# Revit family: GLIDER-SM_AUA03510130001
name_source: partatom
category: Lighting Fixtures
units: mm (PartAtom-declared; Revit-internal decimal feet)

## family parameters
Cut with Voids When Loaded = No
Host = Face
Light Source = Yes
OmniClass Number = 23.80.70.11.21
OmniClass Title = Emergency Lighting
Part Type = Normal
Room Calculation Point = No
Round Connector Dimension = Use Diameter
Shared = No

## types (5) — shared parameters
3D Content Provider = Mepros engineering
Apparent Load = 0 VA
Clevertronics_AS2293 Classification = C0=E4, C90=E4, C180=E2.5, C270=E3.2
Clevertronics_Applicable Standards = AS/NZS3820, CISPR15, AS/NZS2293.3
Clevertronics_Battery = 3.2V 1100mAh
Clevertronics_Battery Type = Lithium Iron Phosphate
Clevertronics_Body/Box (LxWxH mm) = 341mm x 60mm x 215mm
Clevertronics_Charger Method = Intelligent Current Limited Constant Voltage
Clevertronics_Construction = PC/ABS body with PC diffuser
Clevertronics_Diffuser = All pictograph directional inserts included in the box
Clevertronics_Earth Leakage = 0.42
Clevertronics_Emergency Driver = 8003552 : Emergency Driver
Clevertronics_Emergency Node = 8012080 : LED Board
Clevertronics_IP Rating = IP20
Clevertronics_MIC Number = AUA03510130001
Clevertronics_Mounting = Surface Mount, Double Sided
Clevertronics_Operating Mode = Maintained
Clevertronics_Operating Temperature = 1˚C to 40˚C
Clevertronics_Operating Voltage = 240V AC; 50Hz
Clevertronics_Power Consumption = 1.3 Watts (Standby), 2.6 Watts (Max)
Clevertronics_Product Description = Glider Blade Exit, Surface Mount, Trade Series, Picto All, Double Sided
Clevertronics_Replacement Battery = 1560180 : Battery
Clevertronics_Testing System = N/A - Manual test switch
Clevertronics_Viewing Distance = 24m
Clevertronics_Weight = 1.80kg
Color Filter = 16777215
Content Provider URL = https://mepros-eng.com
Description = Glider Blade Exit, Surface Mount, Trade Series, Picto All, Double Sided
Dimming Lamp Color Temperature Shift = <None>
Lamp = 12 x Samsung LED, 50,000 hours
Manufacturer = Clevertronics
Material = Clevertronics_White
Model = GLIDER-SM
Photometric Web File = GLIDER-SM_IESA_E_ll24598a_CIE_202305051049.ies
Product URL = https://clevertronics.com.au
Tilt Angle = 180.00°
URL = https://clevertronics.com.au
zero-valued in all types: Default Elevation

## per-type parameters (varying)
| type | Indication Left | Indication Right | RM Side (DS) | Straight Line (DS) | Straight line |
| Running Man Single | No | No | No | No | Yes |
| Runnign Man Common arrow (double side) | No | No | Yes | No | No |
| Running Man (Double side) | No | No | No | Yes | Yes |
| Running Man Left (Single) | Yes | No | No | No | No |
| Running Man Right (Single) | No | Yes | No | No | No |

## geometry (parser evidence)
native form markers: Blend x2, Sweep x3
no freeform markers — native parametric forms only
